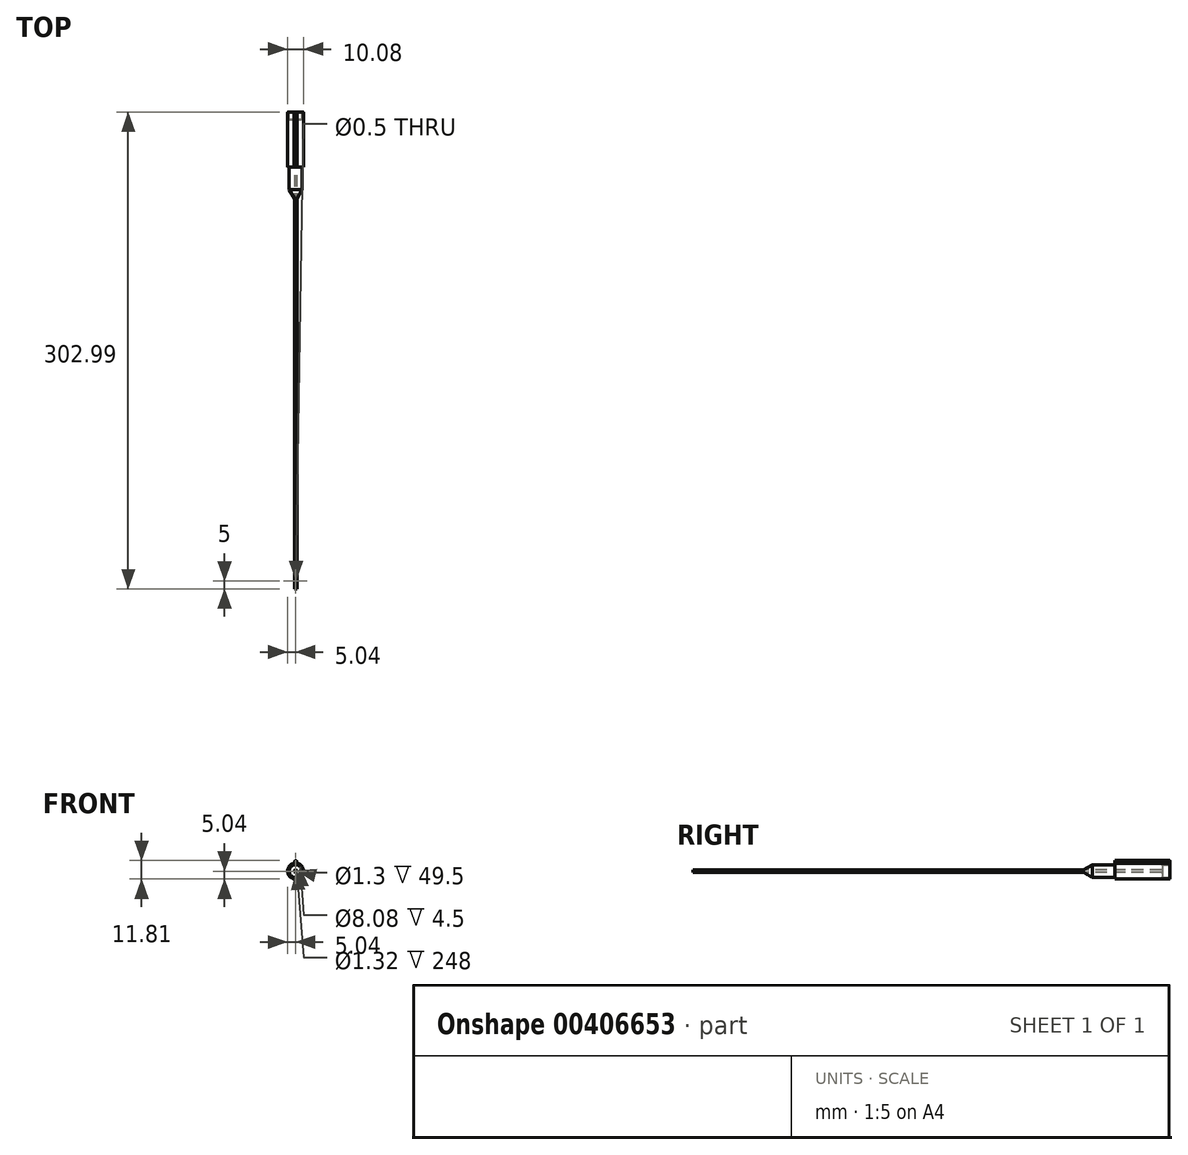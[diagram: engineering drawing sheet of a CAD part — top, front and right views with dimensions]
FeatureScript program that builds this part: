
annotation { "Feature Type Name" : "Feature", "Feature Type Description" : "" }
export const myFeature = defineFeature(function(context is Context, id is Id, definition is map)
    precondition{}
    {
        {
            var Q0;
            Q0=qCreatedBy(makeId("Front.planeOp"),FACE);
            var sketch = newSketch(context, id + "F0", { "sketchPlane" : qUnion([Q0])});
            skCircle(sketch, "E0", {"center": v(0, 0) * mm, "radius": 0.8 * mm});
            skCircle(sketch, "E1.0", {"center": v(0, 0) * mm, "radius": 0.66 * mm});
            skSolve(sketch);
        }
        {
            var Q0;
            Q0 = qSketchRegion(id + "F0", true);
            extrude(context, id + "F1", {"entities" : qUnion([Q0]), "oppositeDirection" : true, "depth" : 248 * mm});
        }
        {
            var Q0;
            Q0=qCreatedBy(makeId("Top.planeOp"),FACE);
            var sketch = newSketch(context, id + "F2", { "sketchPlane" : qUnion([Q0])});
            skCircle(sketch, "E2", {"center": v(0, 5) * mm, "radius": 0.25 * mm});
            skSolve(sketch);
        }
        {
            var Q0;
            Q0 = qSketchRegion(id + "F2", true);
            extrude(context, id + "F3", {"entities" : qUnion([Q0]), "operationType" : NewBodyOperationType.REMOVE, "oppositeDirection" : true, "depth" : -1 * mm});
        }
        {
            var Q0;
            Q0=qCreatedBy(makeId("Right.planeOp"),FACE);
            var sketch = newSketch(context, id + "F4", { "sketchPlane" : qUnion([Q0])});
            skLineSegment(sketch, "E3", {"start": v(247.99, 0.8) * mm, "end": v(253.61, 4.04) * mm});
            skLineSegment(sketch, "E4", {"start": v(253.61, 4.04) * mm, "end": v(267.99, 4.04) * mm});
            skLineSegment(sketch, "E5", {"start": v(267.99, 4.04) * mm, "end": v(267.99, 5.04) * mm});
            skLineSegment(sketch, "E6", {"start": v(267.99, 5.04) * mm, "end": v(302.99, 5.04) * mm});
            skLineSegment(sketch, "E7", {"start": v(302.99, 5.04) * mm, "end": v(302.99, 0.65) * mm});
            skLineSegment(sketch, "E8", {"start": v(302.99, 0.65) * mm, "end": v(247.99, 0.65) * mm});
            skLineSegment(sketch, "E9", {"start": v(247.99, 0.65) * mm, "end": v(247.99, 0.8) * mm});
            skLineSegment(sketch, "E10", {"start": v(0, 0) * mm, "end": v(255.73, 0) * mm});
            skSolve(sketch);
        }
        {
            var Q0;
            Q0=makeQuery(id+"F4.imprint","IMPRINT",FACE,{"disambiguationData":[TD([[makeQuery(id+"F4.imprint","IMPRINT",EDGE,{"derivedFrom":sQuery(id+"F4.wireOp",EDGE,"E3")}),-1.0]])]});
            var Q1;
            Q1=sQuery(id+"F4.wireOp",EDGE,"E10");
            revolve(context, id + "F5", {"entities" : qUnion([Q0]), "axis" : qUnion([Q1]), "revolveType" : RevolveType.FULL});
        }
        {
            var Q0;
            Q0=makeQuery(id+"F5.opRevolve","SWEPT_FACE",FACE,{"disambiguationData":[OSD([sQuery(id+"F4.wireOp",EDGE,"E7")])]});
            cPlane(context, id + "F6", {"entities" : qUnion([Q0]), "cplaneType" : CPlaneType.OFFSET, "offset" : 0 * mm, "width" : 150 * mm, "height" : 150 * mm});
        }
        {
            var Q0;
            Q0=qCreatedBy(id+"F6.planeOp",FACE);
            var sketch = newSketch(context, id + "F7", { "sketchPlane" : qUnion([Q0])});
            skCircle(sketch, "E11", {"center": v(0, 0) * mm, "radius": 4.04 * mm});
            skLineSegment(sketch, "E12", {"start": v(-1, 4.94) * mm, "end": v(1, 4.94) * mm});
            skLineSegment(sketch, "E13", {"start": v(1, 4.94) * mm, "end": v(0, 7.77) * mm});
            skLineSegment(sketch, "E14", {"start": v(0, 7.77) * mm, "end": v(-1, 4.94) * mm});
            skSolve(sketch);
        }
        {
            var Q0;
            Q0=makeQuery(id+"F7.imprint","IMPRINT",FACE,{"disambiguationData":[TD([[makeQuery(id+"F7.imprint","IMPRINT",EDGE,{"derivedFrom":sQuery(id+"F7.wireOp",EDGE,"E11")}),1.0]])]});
            extrude(context, id + "F8", {"entities" : qUnion([Q0]), "operationType" : NewBodyOperationType.REMOVE, "oppositeDirection" : true, "depth" : 5 * mm});
        }
        {
            var Q0;
            Q0=makeQuery(id+"F7.imprint","IMPRINT",FACE,{"disambiguationData":[TD([[makeQuery(id+"F7.imprint","IMPRINT",EDGE,{"derivedFrom":sQuery(id+"F7.wireOp",EDGE,"E12")}),1.0]])]});
            extrude(context, id + "F9", {"entities" : qUnion([Q0]), "operationType" : NewBodyOperationType.ADD, "oppositeDirection" : true, "depth" : 35 * mm});
        }
        {
            var Q0;
            Q0=makeQuery(id+"F5.opRevolve","SWEPT_EDGE",EDGE,{"disambiguationData":[OSD([sQuery(id+"F4.wireOp",EDGE,"E6"),sQuery(id+"F4.wireOp",EDGE,"E7")])]});
            var Q1;
            Q1=makeQuery(id+"F8.boolean.opBoolean","COPY",EDGE,{"derivedFrom":makeQuery(id+"F8.opExtrude","CAP_EDGE",EDGE,{"disambiguationData":[OSD([sQuery(id+"F7.wireOp",EDGE,"E11")])],"isStart":true})});
            var Q2;
            Q2=makeQuery(id+"F8.boolean.opBoolean","COPY",EDGE,{"derivedFrom":makeQuery(id+"F8.opExtrude","CAP_EDGE",EDGE,{"disambiguationData":[OSD([sQuery(id+"F7.wireOp",EDGE,"E11")])],"isStart":false})});
            var Q3;
            Q3=makeQuery(id+"F8.boolean.opBoolean","INTERSECT",EDGE,{"derivedFrom":[makeQuery(id+"F5.opRevolve","SWEPT_FACE",FACE,{"disambiguationData":[OSD([sQuery(id+"F4.wireOp",EDGE,"E8")])]}),makeQuery(id+"F8.opExtrude","CAP_FACE",FACE,{"disambiguationData":[OSD([sQuery(id+"F7.wireOp",EDGE,"E11")])],"isStart":false})]});
            var Q4;
            Q4=makeQuery(id+"F9.opExtrude","CAP_EDGE",EDGE,{"disambiguationData":[OSD([sQuery(id+"F7.wireOp",EDGE,"E14")])],"isStart":true});
            var Q5;
            Q5=makeQuery(id+"F9.opExtrude","CAP_EDGE",EDGE,{"disambiguationData":[OSD([sQuery(id+"F7.wireOp",EDGE,"E13")])],"isStart":true});
            var Q6;
            Q6=makeQuery(id+"F9.opExtrude","SWEPT_EDGE",EDGE,{"disambiguationData":[OSD([sQuery(id+"F7.wireOp",EDGE,"E13"),sQuery(id+"F7.wireOp",EDGE,"E14")])]});
            fillet(context, id + "F10", {"entities" : qUnion([Q0, Q1, Q2, Q3, Q4, Q5, Q6]), "radius" : 0.5 * mm, "tangentPropagation" : true, "allowEdgeOverflow" : false});
        }
    });
